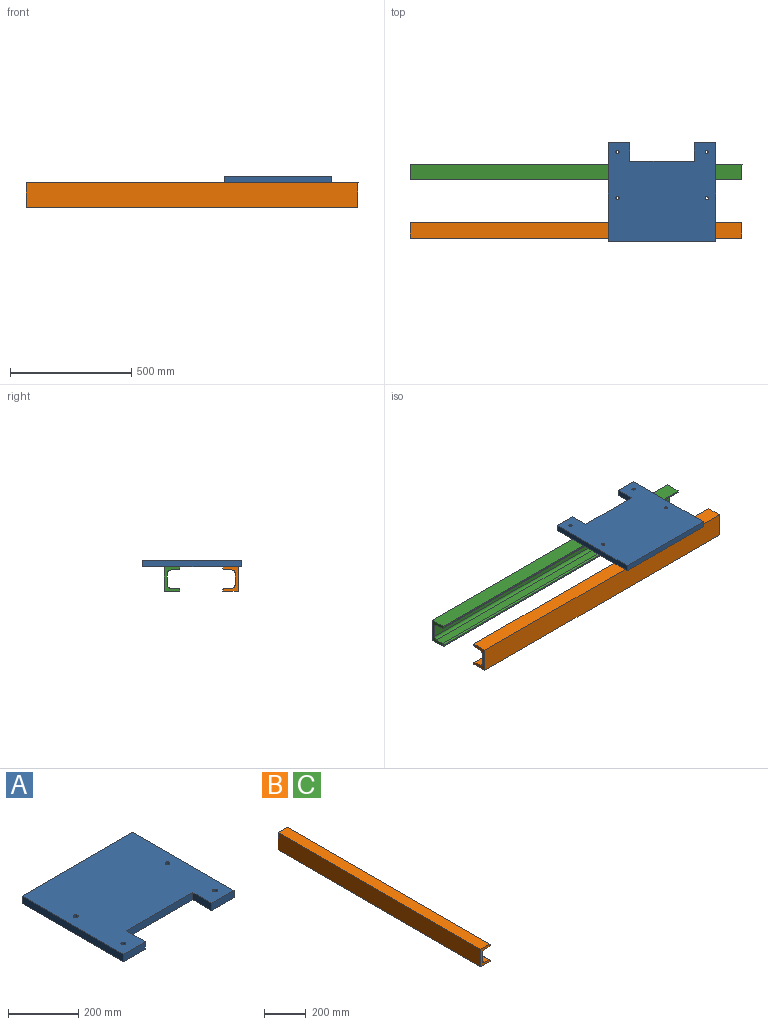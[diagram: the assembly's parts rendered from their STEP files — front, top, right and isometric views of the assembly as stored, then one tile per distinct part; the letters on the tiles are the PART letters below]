
ASSEMBLY  parts=3 mates=2
PART A: 14 faces, bbox 444.5x406.4x25.4 mm
  f0: plane 444.5x25.4mm, normal (0,1,0), area 11290.3mm2, adj f1,f7,f8,f9
  f1: plane 406.4x25.4mm, normal (-1,0,0), area 10322.6mm2, adj f0,f2,f8,f9
  f2: plane 88.9x25.4mm, normal (0,-1,0), area 2258.1mm2, adj f1,f3,f8,f9
  f3: plane 76.2x25.4mm, normal (1,0,0), area 1935.5mm2, adj f2,f4,f8,f9
  f4: plane 266.7x25.4mm, normal (0,-1,0), area 6774.2mm2, adj f3,f5,f8,f9
  f5: plane 76.2x25.4mm, normal (-1,0,0), area 1935.5mm2, adj f4,f6,f8,f9
  f6: plane 88.9x25.4mm, normal (0,-1,0), area 2258.1mm2, adj f5,f7,f8,f9
  f7: plane 406.4x25.4mm, normal (1,0,0), area 10322.6mm2, adj f0,f6,f8,f9
  f8: plane 444.5x406.4mm, normal (0,0,1), area 159750.3mm2, adj f0,f1,f2,f3,f4,f5,f6,f7
  f9: plane 444.5x406.4mm, normal (0,0,-1), area 159750.3mm2, adj f0,f1,f2,f3,f4,f5,f6,f7
  f10: cylinder r=6.75mm len=25.4mm, axis (0,0,-1), area 1076.7mm2, adj f8,f9
  f11: cylinder r=6.75mm len=25.4mm, axis (0,0,-1), area 1076.7mm2, adj f8,f9
  f12: cylinder r=6.75mm len=25.4mm, axis (0,0,-1), area 1076.7mm2, adj f8,f9
  f13: cylinder r=6.75mm len=25.4mm, axis (0,0,-1), area 1076.7mm2, adj f8,f9
PART B: 14 faces, bbox 63.5x1371.6x101.6 mm
  f0: plane 1371.6x63.5mm, normal (0,0,1), area 87096.6mm2, adj f1,f11,f12,f13
  f1: plane 1371.6x101.6mm, normal (-1,0,0), area 139354.6mm2, adj f0,f2,f12,f13
  f2: plane 1371.6x63.5mm, normal (0,0,-1), area 87096.6mm2, adj f1,f3,f12,f13
  f3: plane 1371.6x5.68mm, normal (1,0,0), area 7796.7mm2, adj f2,f4,f12,f13
  f4: cylinder r=5.99mm len=1371.6mm, axis (0,1,0), area 12475.6mm2, adj f3,f5,f12,f13
  f5: plane 1371.6x33.77mm, normal (0.05,0,1), area 46382.7mm2, adj f4,f6,f12,f13
  f6: cylinder r=11.98mm len=1371.6mm, axis (0,1,0), area 24951.1mm2, adj f5,f7,f12,f13
  f7: plane 1371.6x50.8mm, normal (1,0,0), area 69677.3mm2, adj f6,f8,f12,f13
  f8: cylinder r=11.98mm len=1371.6mm, axis (0,1,0), area 24951.1mm2, adj f7,f9,f12,f13
  f9: plane 1371.6x33.77mm, normal (0.05,0,-1), area 46382.7mm2, adj f8,f10,f12,f13
  f10: cylinder r=5.99mm len=1371.6mm, axis (0,1,0), area 12475.6mm2, adj f9,f11,f12,f13
  f11: plane 1371.6x5.68mm, normal (1,0,0), area 7796.7mm2, adj f0,f10,f12,f13
  f12: plane 101.6x63.5mm, normal (0,-1,0), area 2621.5mm2, adj f0,f1,f2,f3,f4,f5,f6,f7
  f13: plane 101.6x63.5mm, normal (0,1,0), area 2621.5mm2, adj f0,f1,f2,f3,f4,f5,f6,f7
PART C: same geometry as B
PLACE A rot(axis=(-1,0,0),180deg) t=(76.22,-112.42,-284.76)mm
PLACE B rot(axis=(0,0,1),90deg) t=(-742.93,-67.97,-360.96)mm
PLACE C rot(axis=(0,0,-1),90deg) t=(628.67,173.33,-360.96)mm
MATE parallel B.f1 <-> C.f1  axis (0,-1,0) through (-742.93,-99.72,-411.76)mm
MATE planar B.f0 <-> A.f8  axis (0,0,1) through (628.67,-99.72,-310.16)mm
